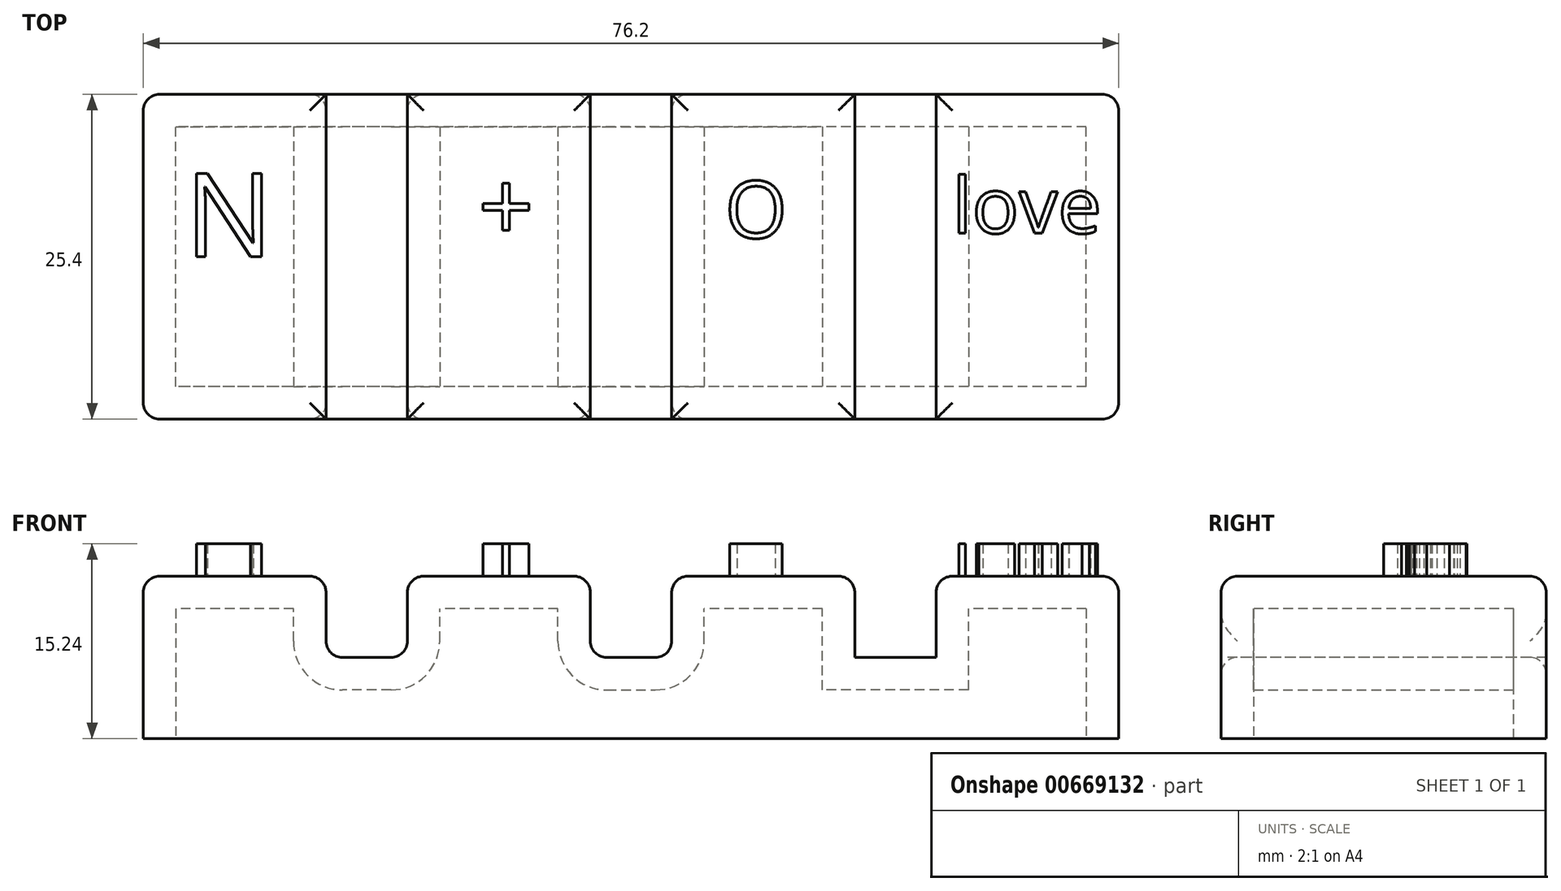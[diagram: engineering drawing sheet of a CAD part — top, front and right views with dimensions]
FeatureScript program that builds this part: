
annotation { "Feature Type Name" : "Feature", "Feature Type Description" : "" }
export const myFeature = defineFeature(function(context is Context, id is Id, definition is map)
    precondition{}
    {
        {
            var Q0;
            Q0=qCreatedBy(makeId("Top.planeOp"),FACE);
            var sketch = newSketch(context, id + "F0", { "sketchPlane" : qUnion([Q0])});
            skLineSegment(sketch, "E0.bottom", {"start": v(38.1, -12.7) * mm, "end": v(-38.1, -12.7) * mm});
            skLineSegment(sketch, "E0.top", {"start": v(38.1, 12.7) * mm, "end": v(-38.1, 12.7) * mm});
            skLineSegment(sketch, "E0.left", {"start": v(38.1, -12.7) * mm, "end": v(38.1, 12.7) * mm});
            skLineSegment(sketch, "E0.right", {"start": v(-38.1, -12.7) * mm, "end": v(-38.1, 12.7) * mm});
            skPoint(sketch, "E0.middle", {"position": v(0, 0) * mm});
            skSolve(sketch);
        }
        {
            var Q0;
            Q0 = qSketchRegion(id + "F0", true);
            extrude(context, id + "F1", {"entities" : qUnion([Q0]), "depth" : 12.7 * mm, "offsetDistance" : 25.4 * mm});
        }
        {
            var Q0;
            Q0=makeQuery(id+"F1.opExtrude","SWEPT_FACE",FACE,{"disambiguationData":[OSD([sQuery(id+"F0.wireOp",EDGE,"E0.bottom")])]});
            var sketch = newSketch(context, id + "F2", { "sketchPlane" : qUnion([Q0])});
            skLineSegment(sketch, "E1", {"start": v(-38.1, 6.35) * mm, "end": v(38.1, 6.35) * mm, "construction": true});
            skLineSegment(sketch, "E2.bottom", {"start": v(3.18, 6.35) * mm, "end": v(-3.17, 6.35) * mm});
            skLineSegment(sketch, "E2.top", {"start": v(3.18, 19.05) * mm, "end": v(-3.17, 19.05) * mm});
            skLineSegment(sketch, "E2.left", {"start": v(3.18, 6.35) * mm, "end": v(3.18, 19.05) * mm});
            skLineSegment(sketch, "E2.right", {"start": v(-3.17, 6.35) * mm, "end": v(-3.17, 19.05) * mm});
            skPoint(sketch, "E2.middle", {"position": v(0, 12.7) * mm});
            skLineSegment(sketch, "E3.bottom", {"start": v(27.28, 6.35) * mm, "end": v(17.48, 6.35) * mm});
            skLineSegment(sketch, "E4.bottom", {"start": v(17.48, 6.35) * mm, "end": v(23.83, 6.35) * mm});
            skLineSegment(sketch, "E4.top", {"start": v(17.48, 19.05) * mm, "end": v(23.83, 19.05) * mm});
            skLineSegment(sketch, "E4.left", {"start": v(17.48, 6.35) * mm, "end": v(17.48, 19.05) * mm});
            skLineSegment(sketch, "E4.right", {"start": v(23.83, 6.35) * mm, "end": v(23.83, 19.05) * mm});
            skPoint(sketch, "E4.middle", {"position": v(20.65, 12.7) * mm});
            skLineSegment(sketch, "E5.bottom", {"start": v(-23.83, 6.35) * mm, "end": v(-17.48, 6.35) * mm});
            skLineSegment(sketch, "E5.top", {"start": v(-23.83, 19.05) * mm, "end": v(-17.48, 19.05) * mm});
            skLineSegment(sketch, "E5.left", {"start": v(-23.83, 6.35) * mm, "end": v(-23.83, 19.05) * mm});
            skLineSegment(sketch, "E5.right", {"start": v(-17.48, 6.35) * mm, "end": v(-17.48, 19.05) * mm});
            skPoint(sketch, "E5.middle", {"position": v(-20.65, 12.7) * mm});
            skSolve(sketch);
        }
        {
            var Q0;
            Q0 = qSketchRegion(id + "F2", true);
            extrude(context, id + "F3", {"entities" : qUnion([Q0]), "operationType" : NewBodyOperationType.REMOVE, "endBound" : BoundingType.THROUGH_ALL, "oppositeDirection" : true, "depth" : 25.4 * mm, "offsetDistance" : 25.4 * mm});
        }
        {
            var Q0;
            {var subQ0=sQuery(id+"F0.wireOp",EDGE,"E0.bottom");var subQ1=sQuery(id+"F0.wireOp",EDGE,"E0.right");var subQ2=sQuery(id+"F0.wireOp",EDGE,"E0.top");Q0=makeQuery(id+"F3.boolean.opBoolean","SPLIT",FACE,{"disambiguationData":[TD([makeQuery(id+"F1.opExtrude","SWEPT_FACE",FACE,{"disambiguationData":[OSD([subQ1])]})])],"derivedFrom":makeQuery(id+"F1.opExtrude","CAP_FACE",FACE,{"disambiguationData":[OSD([subQ0,subQ2,sQuery(id+"F0.wireOp",EDGE,"E0.left"),subQ1])],"isStart":false})});}
            var Q1;
            {var subQ0=sQuery(id+"F0.wireOp",EDGE,"E0.bottom");var subQ1=sQuery(id+"F0.wireOp",EDGE,"E0.top");Q1=makeQuery(id+"F3.boolean.opBoolean","SPLIT",FACE,{"disambiguationData":[TD([makeQuery(id+"F3.opExtrude","SWEPT_FACE",FACE,{"disambiguationData":[OSD([sQuery(id+"F2.wireOp",EDGE,"E2.right")])]})])],"derivedFrom":makeQuery(id+"F1.opExtrude","CAP_FACE",FACE,{"disambiguationData":[OSD([subQ0,subQ1,sQuery(id+"F0.wireOp",EDGE,"E0.left"),sQuery(id+"F0.wireOp",EDGE,"E0.right")])],"isStart":false})});}
            var Q2;
            {var subQ0=sQuery(id+"F0.wireOp",EDGE,"E0.bottom");var subQ1=sQuery(id+"F0.wireOp",EDGE,"E0.top");Q2=makeQuery(id+"F3.boolean.opBoolean","SPLIT",FACE,{"disambiguationData":[TD([makeQuery(id+"F3.opExtrude","SWEPT_FACE",FACE,{"disambiguationData":[OSD([sQuery(id+"F2.wireOp",EDGE,"E2.left")])]})])],"derivedFrom":makeQuery(id+"F1.opExtrude","CAP_FACE",FACE,{"disambiguationData":[OSD([subQ0,subQ1,sQuery(id+"F0.wireOp",EDGE,"E0.left"),sQuery(id+"F0.wireOp",EDGE,"E0.right")])],"isStart":false})});}
            var Q3;
            {var subQ0=sQuery(id+"F0.wireOp",EDGE,"E0.bottom");var subQ1=sQuery(id+"F0.wireOp",EDGE,"E0.top");var subQ2=sQuery(id+"F0.wireOp",EDGE,"E0.left");Q3=makeQuery(id+"F3.boolean.opBoolean","SPLIT",FACE,{"disambiguationData":[TD([makeQuery(id+"F1.opExtrude","SWEPT_FACE",FACE,{"disambiguationData":[OSD([subQ2])]})])],"derivedFrom":makeQuery(id+"F1.opExtrude","CAP_FACE",FACE,{"disambiguationData":[OSD([subQ0,subQ1,subQ2,sQuery(id+"F0.wireOp",EDGE,"E0.right")])],"isStart":false})});}
            var Q4;
            Q4=makeQuery(id+"F3.boolean.opBoolean","COPY",FACE,{"derivedFrom":makeQuery(id+"F3.opExtrude","SWEPT_FACE",FACE,{"disambiguationData":[OSD([sQuery(id+"F2.wireOp",EDGE,"E4.bottom")])]})});
            var Q5;
            Q5=makeQuery(id+"F3.boolean.opBoolean","COPY",FACE,{"derivedFrom":makeQuery(id+"F3.opExtrude","SWEPT_FACE",FACE,{"disambiguationData":[OSD([sQuery(id+"F2.wireOp",EDGE,"E2.bottom")])]})});
            var Q6;
            Q6=makeQuery(id+"F3.boolean.opBoolean","COPY",FACE,{"derivedFrom":makeQuery(id+"F3.opExtrude","SWEPT_FACE",FACE,{"disambiguationData":[OSD([sQuery(id+"F2.wireOp",EDGE,"E5.bottom")])]})});
            var Q7;
            Q7=makeQuery(id+"F1.opExtrude","SWEPT_EDGE",EDGE,{"disambiguationData":[OSD([sQuery(id+"F0.wireOp",EDGE,"E0.bottom"),sQuery(id+"F0.wireOp",EDGE,"E0.left")])]});
            var Q8;
            Q8=makeQuery(id+"F1.opExtrude","SWEPT_EDGE",EDGE,{"disambiguationData":[OSD([sQuery(id+"F0.wireOp",EDGE,"E0.top"),sQuery(id+"F0.wireOp",EDGE,"E0.left")])]});
            var Q9;
            Q9=makeQuery(id+"F1.opExtrude","SWEPT_EDGE",EDGE,{"disambiguationData":[OSD([sQuery(id+"F0.wireOp",EDGE,"E0.bottom"),sQuery(id+"F0.wireOp",EDGE,"E0.right")])]});
            var Q10;
            Q10=makeQuery(id+"F1.opExtrude","SWEPT_EDGE",EDGE,{"disambiguationData":[OSD([sQuery(id+"F0.wireOp",EDGE,"E0.top"),sQuery(id+"F0.wireOp",EDGE,"E0.right")])]});
            fillet(context, id + "F4", {"entities" : qUnion([Q0, Q1, Q2, Q3, Q4, Q5, Q6, Q7, Q8, Q9, Q10]), "radius" : 1.27 * mm, "tangentPropagation" : true, "allowEdgeOverflow" : false});
        }
        {
            var Q0;
            Q0=makeQuery(id+"F1.opExtrude","CAP_FACE",FACE,{"disambiguationData":[OSD([sQuery(id+"F0.wireOp",EDGE,"E0.bottom"),sQuery(id+"F0.wireOp",EDGE,"E0.top"),sQuery(id+"F0.wireOp",EDGE,"E0.left"),sQuery(id+"F0.wireOp",EDGE,"E0.right")])],"isStart":true});
            shell(context, id + "F5", {"entities" : qUnion([Q0]), "thickness" : 2.54 * mm});
        }
        {
            var Q0;
            {var subQ0=sQuery(id+"F0.wireOp",EDGE,"E0.bottom");var subQ1=sQuery(id+"F0.wireOp",EDGE,"E0.right");var subQ2=sQuery(id+"F0.wireOp",EDGE,"E0.top");Q0=makeQuery(id+"F3.boolean.opBoolean","SPLIT",FACE,{"disambiguationData":[TD([makeQuery(id+"F1.opExtrude","SWEPT_FACE",FACE,{"disambiguationData":[OSD([subQ1])]})])],"derivedFrom":makeQuery(id+"F1.opExtrude","CAP_FACE",FACE,{"disambiguationData":[OSD([subQ0,subQ2,sQuery(id+"F0.wireOp",EDGE,"E0.left"),subQ1])],"isStart":false})});}
            var sketch = newSketch(context, id + "F6", { "sketchPlane" : qUnion([Q0])});
            skText(sketch, "E6", { "text": "N", "fontName": "OpenSans-Regular.ttf"});
            const initialGuessF6  = {"E6": [-0.03483, 0, 1, 0, 0.00656]};
            skSetInitialGuess(sketch, initialGuessF6);
            skSolve(sketch);
        }
        {
            var Q0;
            {var subQ0=sQuery(id+"F0.wireOp",EDGE,"E0.bottom");var subQ1=sQuery(id+"F0.wireOp",EDGE,"E0.top");Q0=makeQuery(id+"F3.boolean.opBoolean","SPLIT",FACE,{"disambiguationData":[TD([makeQuery(id+"F3.opExtrude","SWEPT_FACE",FACE,{"disambiguationData":[OSD([sQuery(id+"F2.wireOp",EDGE,"E2.right")])]})])],"derivedFrom":makeQuery(id+"F1.opExtrude","CAP_FACE",FACE,{"disambiguationData":[OSD([subQ0,subQ1,sQuery(id+"F0.wireOp",EDGE,"E0.left"),sQuery(id+"F0.wireOp",EDGE,"E0.right")])],"isStart":false})});}
            var sketch = newSketch(context, id + "F7", { "sketchPlane" : qUnion([Q0])});
            skText(sketch, "E7", { "text": "+\n", "fontName": "OpenSans-Regular.ttf"});
            const initialGuessF7  = {"E7": [-0.01194, 0.00121, 1, 0, 0.00547]};
            skSetInitialGuess(sketch, initialGuessF7);
            skSolve(sketch);
        }
        {
            var Q0;
            {var subQ0=sQuery(id+"F0.wireOp",EDGE,"E0.bottom");var subQ1=sQuery(id+"F0.wireOp",EDGE,"E0.top");Q0=makeQuery(id+"F3.boolean.opBoolean","SPLIT",FACE,{"disambiguationData":[TD([makeQuery(id+"F3.opExtrude","SWEPT_FACE",FACE,{"disambiguationData":[OSD([sQuery(id+"F2.wireOp",EDGE,"E2.left")])]})])],"derivedFrom":makeQuery(id+"F1.opExtrude","CAP_FACE",FACE,{"disambiguationData":[OSD([subQ0,subQ1,sQuery(id+"F0.wireOp",EDGE,"E0.left"),sQuery(id+"F0.wireOp",EDGE,"E0.right")])],"isStart":false})});}
            var sketch = newSketch(context, id + "F8", { "sketchPlane" : qUnion([Q0])});
            skText(sketch, "E8", { "text": "O", "fontName": "OpenSans-Regular.ttf"});
            const initialGuessF8  = {"E8": [0.00734, 0.00146, 1, 0, 0.00448]};
            skSetInitialGuess(sketch, initialGuessF8);
            skSolve(sketch);
        }
        {
            var Q0;
            {var subQ0=sQuery(id+"F0.wireOp",EDGE,"E0.bottom");var subQ1=sQuery(id+"F0.wireOp",EDGE,"E0.top");var subQ2=sQuery(id+"F0.wireOp",EDGE,"E0.left");Q0=makeQuery(id+"F3.boolean.opBoolean","SPLIT",FACE,{"disambiguationData":[TD([makeQuery(id+"F1.opExtrude","SWEPT_FACE",FACE,{"disambiguationData":[OSD([subQ2])]})])],"derivedFrom":makeQuery(id+"F1.opExtrude","CAP_FACE",FACE,{"disambiguationData":[OSD([subQ0,subQ1,subQ2,sQuery(id+"F0.wireOp",EDGE,"E0.right")])],"isStart":false})});}
            var sketch = newSketch(context, id + "F9", { "sketchPlane" : qUnion([Q0])});
            skText(sketch, "E9", { "text": "love\n", "fontName": "OpenSans-Regular.ttf"});
            const initialGuessF9  = {"E9": [0.0251, 0.00183, 1, 0, 0.00437]};
            skSetInitialGuess(sketch, initialGuessF9);
            skSolve(sketch);
        }
        {
            var Q0;
            Q0 = qSketchRegion(id + "F6", true);
            extrude(context, id + "F10", {"entities" : qUnion([Q0]), "operationType" : NewBodyOperationType.ADD, "depth" : 2.54 * mm, "offsetDistance" : 25.4 * mm});
        }
        {
            var Q0;
            Q0 = qSketchRegion(id + "F7", true);
            extrude(context, id + "F11", {"entities" : qUnion([Q0]), "operationType" : NewBodyOperationType.ADD, "depth" : 2.54 * mm, "offsetDistance" : 25.4 * mm});
        }
        {
            var Q0;
            Q0 = qSketchRegion(id + "F8", true);
            extrude(context, id + "F12", {"entities" : qUnion([Q0]), "operationType" : NewBodyOperationType.ADD, "depth" : 2.54 * mm, "offsetDistance" : 25.4 * mm});
        }
        {
            var Q0;
            Q0 = qSketchRegion(id + "F9", true);
            extrude(context, id + "F13", {"entities" : qUnion([Q0]), "operationType" : NewBodyOperationType.ADD, "depth" : 2.54 * mm, "offsetDistance" : 25.4 * mm});
        }
    });
